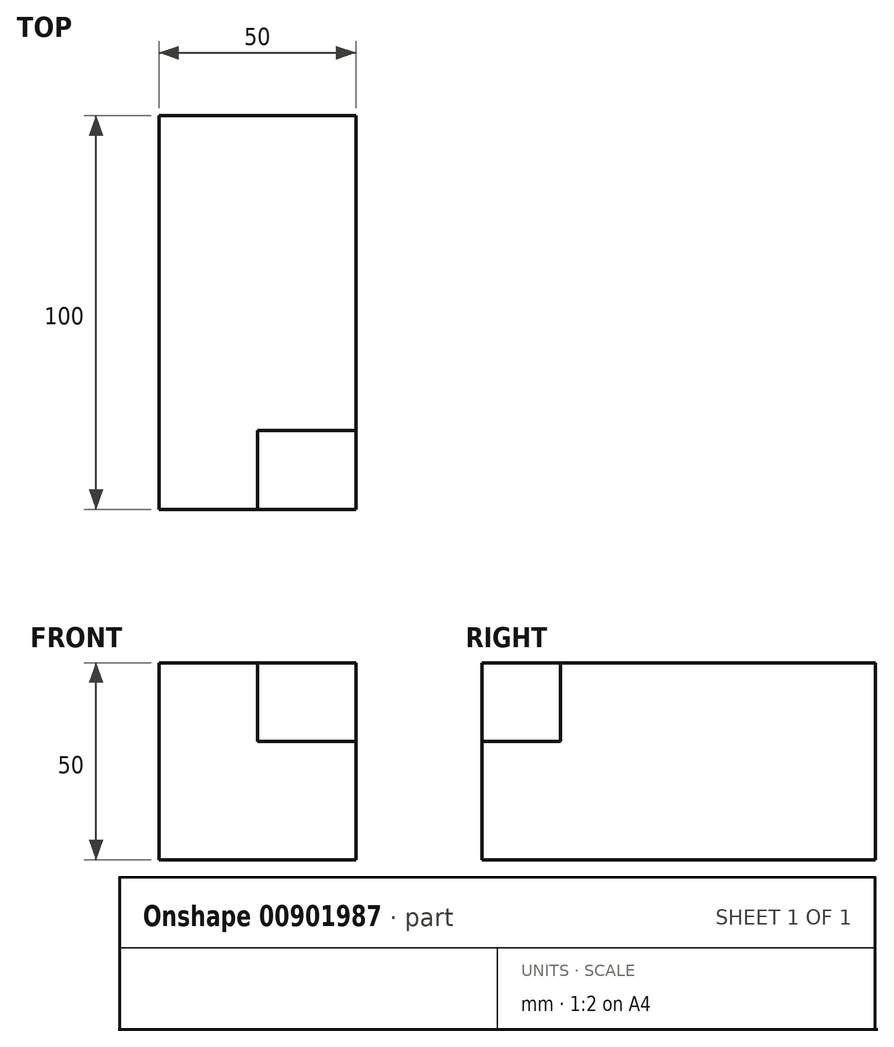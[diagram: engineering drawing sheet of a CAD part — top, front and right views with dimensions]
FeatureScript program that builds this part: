
annotation { "Feature Type Name" : "Feature", "Feature Type Description" : "" }
export const myFeature = defineFeature(function(context is Context, id is Id, definition is map)
    precondition{}
    {
        {
            var Q0;
            Q0=qCreatedBy(makeId("Front.planeOp"),FACE);
            var sketch = newSketch(context, id + "F0", { "sketchPlane" : qUnion([Q0])});
            skLineSegment(sketch, "E0.bottom", {"start": v(25, 25) * mm, "end": v(-25, 25) * mm});
            skLineSegment(sketch, "E0.top", {"start": v(25, -25) * mm, "end": v(-25, -25) * mm});
            skLineSegment(sketch, "E0.left", {"start": v(25, 25) * mm, "end": v(25, -25) * mm});
            skLineSegment(sketch, "E0.right", {"start": v(-25, 25) * mm, "end": v(-25, -25) * mm});
            skPoint(sketch, "E0.middle", {"position": v(0, 0) * mm});
            skSolve(sketch);
        }
        {
            var Q0;
            Q0 = qSketchRegion(id + "F0", true);
            extrude(context, id + "F1", {"entities" : qUnion([Q0]), "endBound" : BoundingType.SYMMETRIC, "depth" : 100 * mm, "offsetDistance" : 25 * mm});
        }
        {
            var Q0;
            Q0=makeQuery(id+"F1.opExtrude","SWEPT_FACE",FACE,{"disambiguationData":[OSD([sQuery(id+"F0.wireOp",EDGE,"E0.left")])]});
            var sketch = newSketch(context, id + "F2", { "sketchPlane" : qUnion([Q0])});
            skLineSegment(sketch, "E1.bottom", {"start": v(-50, 25) * mm, "end": v(-30, 25) * mm});
            skLineSegment(sketch, "E1.top", {"start": v(-50, 5) * mm, "end": v(-30, 5) * mm});
            skLineSegment(sketch, "E1.left", {"start": v(-50, 25) * mm, "end": v(-50, 5) * mm});
            skLineSegment(sketch, "E1.right", {"start": v(-30, 25) * mm, "end": v(-30, 5) * mm});
            skSolve(sketch);
        }
        {
            var Q0;
            Q0=makeQuery(id+"F2.imprint","IMPRINT",FACE,{"disambiguationData":[TD([[makeQuery(id+"F2.imprint","IMPRINT",EDGE,{"derivedFrom":sQuery(id+"F2.wireOp",EDGE,"E1.bottom")}),-1.0]])]});
            extrude(context, id + "F3", {"entities" : qUnion([Q0]), "operationType" : NewBodyOperationType.REMOVE, "oppositeDirection" : true, "depth" : 25 * mm, "offsetDistance" : 25 * mm});
        }
    });
